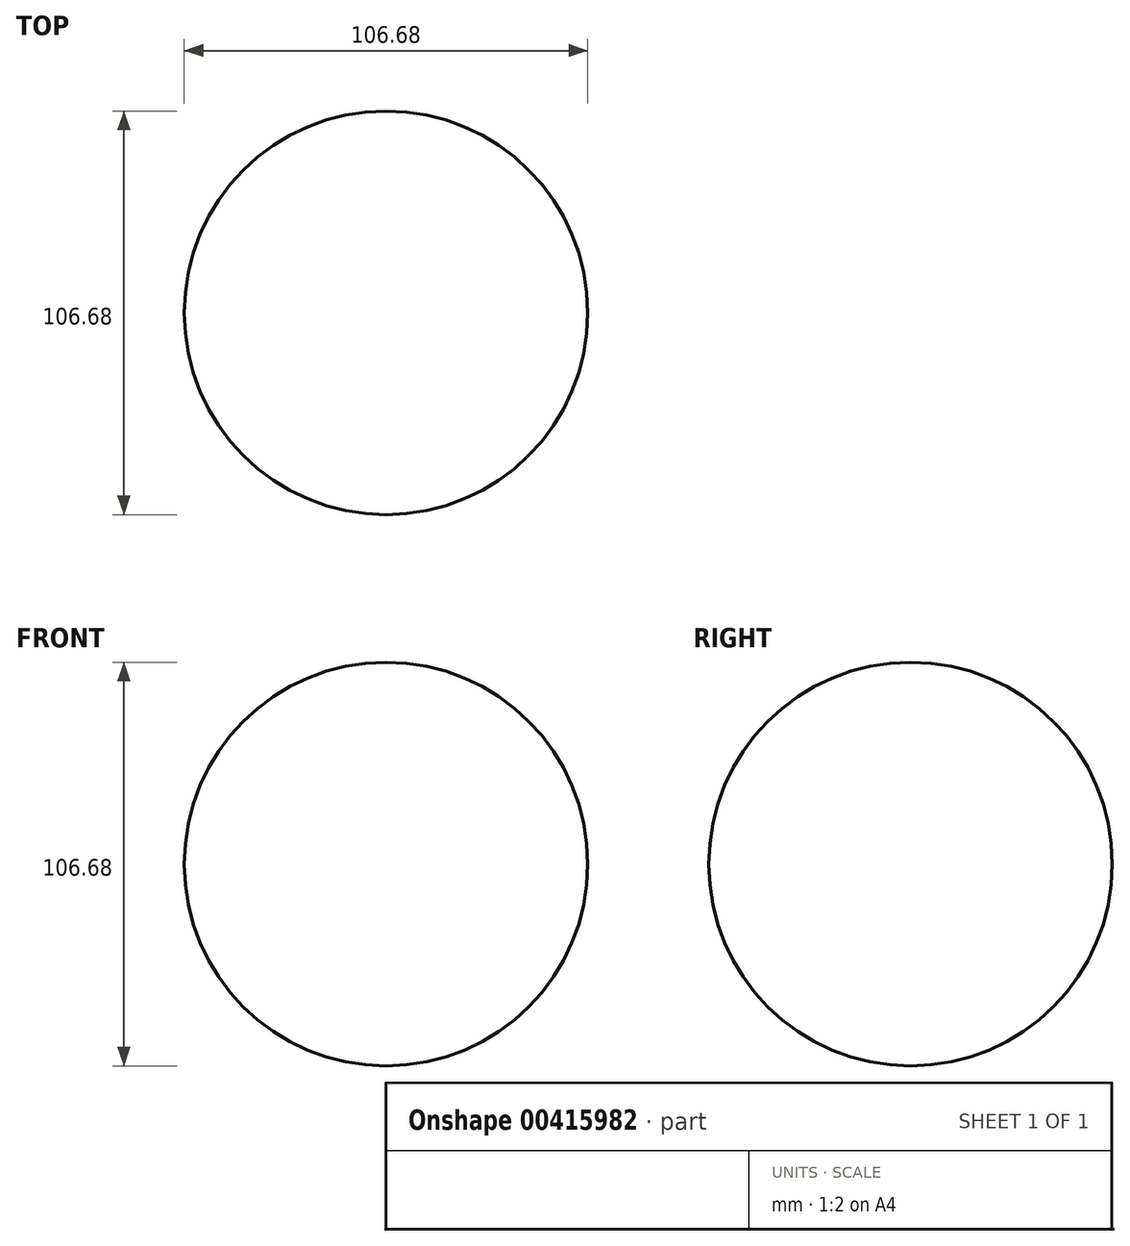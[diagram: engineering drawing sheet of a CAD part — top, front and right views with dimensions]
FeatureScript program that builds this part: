
annotation { "Feature Type Name" : "Feature", "Feature Type Description" : "" }
export const myFeature = defineFeature(function(context is Context, id is Id, definition is map)
    precondition{}
    {
        {
            var Q0;
            Q0=qCreatedBy(makeId("Front.planeOp"),FACE);
            var sketch = newSketch(context, id + "F0", { "sketchPlane" : qUnion([Q0])});
            skArc(sketch, "E0", {"start": v(0, -53.34) * mm, "mid": v(53.34, 0) * mm, "end": v(0, 53.34) * mm});
            skPoint(sketch, "E1", {"position": v(53.34, 0) * mm});
            skLineSegment(sketch, "E2", {"start": v(0, 30.98) * mm, "end": v(0, -31.28) * mm});
            skLineSegment(sketch, "E3", {"start": v(0, 53.34) * mm, "end": v(0, -53.34) * mm});
            skSolve(sketch);
        }
        {
            var Q0;
            {var subQ0=sQuery(id+"F0.wireOp",EDGE,"E0");Q0=makeQuery(id+"F0.imprint","IMPRINT",FACE,{"disambiguationData":[TD([[makeQuery(id+"F0.imprint","IMPRINT",EDGE,{"derivedFrom":subQ0}),1.0]])]});}
            var Q1;
            Q1=sQuery(id+"F0.wireOp",EDGE,"E3");
            revolve(context, id + "F1", {"entities" : qUnion([Q0]), "axis" : qUnion([Q1]), "revolveType" : RevolveType.FULL});
        }
    });
